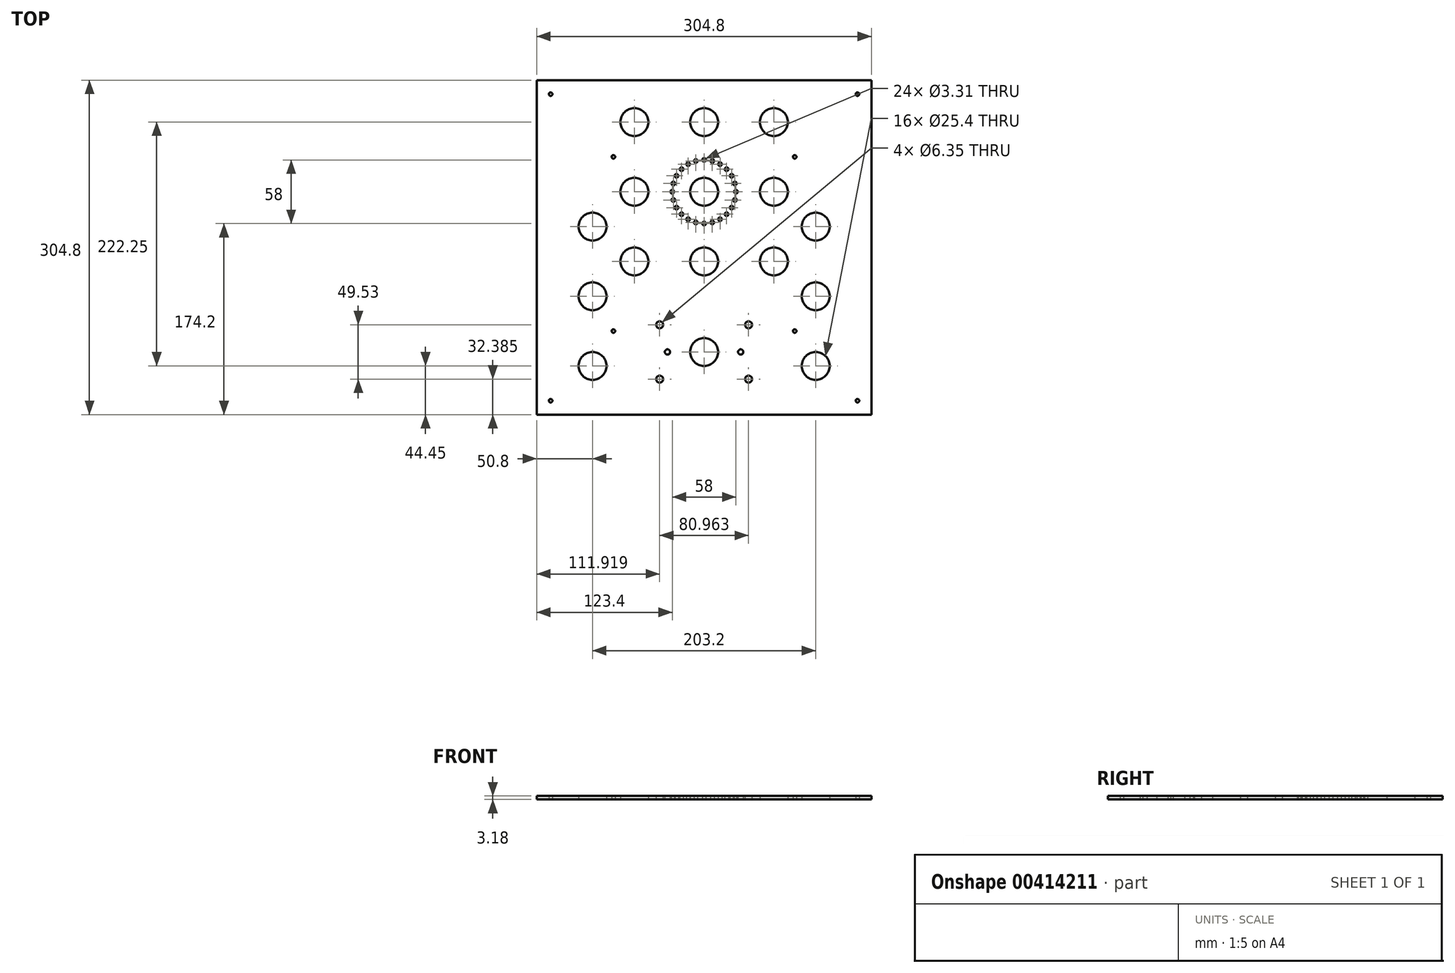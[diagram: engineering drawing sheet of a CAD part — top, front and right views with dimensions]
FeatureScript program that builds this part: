
annotation { "Feature Type Name" : "Feature", "Feature Type Description" : "" }
export const myFeature = defineFeature(function(context is Context, id is Id, definition is map)
    precondition{}
    {
        {
            var Q0;
            Q0=qCreatedBy(makeId("Top.planeOp"),FACE);
            var sketch = newSketch(context, id + "F0", { "sketchPlane" : qUnion([Q0])});
            skLineSegment(sketch, "E0.bottom", {"start": v(152.4, -152.4) * mm, "end": v(-152.4, -152.4) * mm});
            skLineSegment(sketch, "E0.top", {"start": v(152.4, 152.4) * mm, "end": v(-152.4, 152.4) * mm});
            skLineSegment(sketch, "E0.left", {"start": v(152.4, -152.4) * mm, "end": v(152.4, 152.4) * mm});
            skLineSegment(sketch, "E0.right", {"start": v(-152.4, -152.4) * mm, "end": v(-152.4, 152.4) * mm});
            skPoint(sketch, "E0.middle", {"position": v(0, 0) * mm});
            skCircle(sketch, "E1", {"center": v(0, -95.25) * mm, "radius": 12.7 * mm});
            skLineSegment(sketch, "E2.bottom", {"start": v(50.8, -133.35) * mm, "end": v(-50.8, -133.35) * mm, "construction": true});
            skLineSegment(sketch, "E2.top", {"start": v(50.8, -57.15) * mm, "end": v(-50.8, -57.15) * mm, "construction": true});
            skLineSegment(sketch, "E2.left", {"start": v(50.8, -133.35) * mm, "end": v(50.8, -57.15) * mm, "construction": true});
            skLineSegment(sketch, "E2.right", {"start": v(-50.8, -133.35) * mm, "end": v(-50.8, -57.15) * mm, "construction": true});
            skLineSegment(sketch, "E3.bottom", {"start": v(146.05, -146.05) * mm, "end": v(-146.05, -146.05) * mm, "construction": true});
            skLineSegment(sketch, "E3.top", {"start": v(146.05, 146.05) * mm, "end": v(-146.05, 146.05) * mm, "construction": true});
            skLineSegment(sketch, "E3.left", {"start": v(146.05, -146.05) * mm, "end": v(146.05, 146.05) * mm, "construction": true});
            skLineSegment(sketch, "E3.right", {"start": v(-146.05, -146.05) * mm, "end": v(-146.05, 146.05) * mm, "construction": true});
            skCircle(sketch, "E4", {"center": v(-63.5, 114.3) * mm, "radius": 12.7 * mm});
            skCircle(sketch, "E5.0.1.0", {"center": v(-63.5, 50.8) * mm, "radius": 12.7 * mm});
            skCircle(sketch, "E5.0.2.0", {"center": v(-63.5, -12.7) * mm, "radius": 12.7 * mm});
            skCircle(sketch, "E5.1.0.0", {"center": v(0, 114.3) * mm, "radius": 12.7 * mm});
            skCircle(sketch, "E5.1.1.0", {"center": v(0, 50.8) * mm, "radius": 12.7 * mm});
            skCircle(sketch, "E5.1.2.0", {"center": v(0, -12.7) * mm, "radius": 12.7 * mm});
            skCircle(sketch, "E5.2.0.0", {"center": v(63.5, 114.3) * mm, "radius": 12.7 * mm});
            skCircle(sketch, "E5.2.1.0", {"center": v(63.5, 50.8) * mm, "radius": 12.7 * mm});
            skCircle(sketch, "E5.2.2.0", {"center": v(63.5, -12.7) * mm, "radius": 12.7 * mm});
            skLineSegment(sketch, "E5.direction1", {"start": v(-63.5, 114.3) * mm, "end": v(0, 114.3) * mm, "construction": true});
            skLineSegment(sketch, "E5.direction2", {"start": v(-63.5, 114.3) * mm, "end": v(-63.5, 50.8) * mm, "construction": true});
            skCircle(sketch, "E6", {"center": v(-101.6, -107.95) * mm, "radius": 12.7 * mm});
            skCircle(sketch, "E7.0.1.0", {"center": v(-101.6, -44.45) * mm, "radius": 12.7 * mm});
            skCircle(sketch, "E7.0.2.0", {"center": v(-101.6, 19.05) * mm, "radius": 12.7 * mm});
            skCircle(sketch, "E7.1.0.0", {"center": v(101.6, -107.95) * mm, "radius": 12.7 * mm});
            skCircle(sketch, "E7.1.1.0", {"center": v(101.6, -44.45) * mm, "radius": 12.7 * mm});
            skCircle(sketch, "E7.1.2.0", {"center": v(101.6, 19.05) * mm, "radius": 12.7 * mm});
            skLineSegment(sketch, "E7.direction1", {"start": v(-101.6, -107.95) * mm, "end": v(101.6, -107.95) * mm, "construction": true});
            skLineSegment(sketch, "E7.direction2", {"start": v(-101.6, -107.95) * mm, "end": v(-101.6, -44.45) * mm, "construction": true});
            skPoint(sketch, "E8", {"position": v(0, -107.95) * mm});
            skCircle(sketch, "E9", {"center": v(0, 50.8) * mm, "radius": 33 * mm, "construction": true});
            skCircle(sketch, "E10", {"center": v(0, 50.8) * mm, "radius": 25.5 * mm, "construction": true});
            skCircle(sketch, "E11", {"center": v(0, 79.8) * mm, "radius": 1.66 * mm});
            skCircle(sketch, "E12.1.0", {"center": v(-7.5, 78.81) * mm, "radius": 1.66 * mm});
            skCircle(sketch, "E12.2.0", {"center": v(-14.5, 75.91) * mm, "radius": 1.66 * mm});
            skCircle(sketch, "E12.3.0", {"center": v(-20.5, 71.3) * mm, "radius": 1.66 * mm});
            skCircle(sketch, "E12.4.0", {"center": v(-25.11, 65.3) * mm, "radius": 1.66 * mm});
            skCircle(sketch, "E12.5.0", {"center": v(-28.01, 58.3) * mm, "radius": 1.66 * mm});
            skCircle(sketch, "E12.6.0", {"center": v(-29, 50.8) * mm, "radius": 1.66 * mm});
            skCircle(sketch, "E12.7.0", {"center": v(-28.01, 43.3) * mm, "radius": 1.66 * mm});
            skCircle(sketch, "E12.8.0", {"center": v(-25.11, 36.3) * mm, "radius": 1.66 * mm});
            skCircle(sketch, "E12.9.0", {"center": v(-20.5, 30.3) * mm, "radius": 1.66 * mm});
            skCircle(sketch, "E12.10.0", {"center": v(-14.5, 25.69) * mm, "radius": 1.66 * mm});
            skCircle(sketch, "E12.11.0", {"center": v(-7.5, 22.79) * mm, "radius": 1.66 * mm});
            skCircle(sketch, "E12.12.0", {"center": v(0, 21.8) * mm, "radius": 1.66 * mm});
            skCircle(sketch, "E12.13.0", {"center": v(7.5, 22.79) * mm, "radius": 1.66 * mm});
            skCircle(sketch, "E12.14.0", {"center": v(14.5, 25.69) * mm, "radius": 1.66 * mm});
            skCircle(sketch, "E12.15.0", {"center": v(20.5, 30.3) * mm, "radius": 1.66 * mm});
            skCircle(sketch, "E12.16.0", {"center": v(25.11, 36.3) * mm, "radius": 1.66 * mm});
            skCircle(sketch, "E12.17.0", {"center": v(28.01, 43.3) * mm, "radius": 1.66 * mm});
            skCircle(sketch, "E12.18.0", {"center": v(29, 50.8) * mm, "radius": 1.66 * mm});
            skCircle(sketch, "E12.19.0", {"center": v(28.01, 58.3) * mm, "radius": 1.66 * mm});
            skCircle(sketch, "E12.20.0", {"center": v(25.11, 65.3) * mm, "radius": 1.66 * mm});
            skCircle(sketch, "E12.21.0", {"center": v(20.5, 71.3) * mm, "radius": 1.66 * mm});
            skCircle(sketch, "E12.22.0", {"center": v(14.5, 75.91) * mm, "radius": 1.66 * mm});
            skCircle(sketch, "E12.23.0", {"center": v(7.5, 78.81) * mm, "radius": 1.66 * mm});
            skLineSegment(sketch, "E13", {"start": v(-33.34, -95.25) * mm, "end": v(33.34, -95.25) * mm, "construction": true});
            skCircle(sketch, "E14", {"center": v(-33.34, -95.25) * mm, "radius": 2.38 * mm});
            skCircle(sketch, "E15", {"center": v(33.34, -95.25) * mm, "radius": 2.38 * mm});
            skLineSegment(sketch, "E16", {"start": v(-40.48, -70.49) * mm, "end": v(-40.48, -120.02) * mm, "construction": true});
            skLineSegment(sketch, "E17", {"start": v(-40.48, -120.02) * mm, "end": v(40.48, -120.02) * mm, "construction": true});
            skLineSegment(sketch, "E18", {"start": v(40.48, -120.02) * mm, "end": v(40.48, -70.49) * mm, "construction": true});
            skLineSegment(sketch, "E19", {"start": v(40.48, -70.49) * mm, "end": v(-40.48, -70.49) * mm, "construction": true});
            skPoint(sketch, "E20", {"position": v(0, -70.49) * mm});
            skPoint(sketch, "E21", {"position": v(-40.48, -95.25) * mm});
            skCircle(sketch, "E22", {"center": v(-40.48, -70.49) * mm, "radius": 3.18 * mm});
            skCircle(sketch, "E23", {"center": v(40.48, -70.49) * mm, "radius": 3.18 * mm});
            skCircle(sketch, "E24", {"center": v(40.48, -120.02) * mm, "radius": 3.18 * mm});
            skCircle(sketch, "E25", {"center": v(-40.48, -120.02) * mm, "radius": 3.18 * mm});
            skLineSegment(sketch, "E26.bottom", {"start": v(-82.55, 82.55) * mm, "end": v(82.55, 82.55) * mm, "construction": true});
            skLineSegment(sketch, "E26.top", {"start": v(-82.55, -76.2) * mm, "end": v(82.55, -76.2) * mm, "construction": true});
            skLineSegment(sketch, "E26.left", {"start": v(-82.55, 82.55) * mm, "end": v(-82.55, -76.2) * mm, "construction": true});
            skLineSegment(sketch, "E26.right", {"start": v(82.55, 82.55) * mm, "end": v(82.55, -76.2) * mm, "construction": true});
            skPoint(sketch, "E27", {"position": v(0, 82.55) * mm});
            skPoint(sketch, "E28", {"position": v(-101.6, -76.2) * mm});
            skPoint(sketch, "E29", {"position": v(-63.5, 82.55) * mm});
            skLineSegment(sketch, "E30", {"start": v(-63.5, 50.8) * mm, "end": v(-63.5, -12.7) * mm, "construction": true});
            skLineSegment(sketch, "E31", {"start": v(-101.6, 19.05) * mm, "end": v(-63.5, 19.05) * mm, "construction": true});
            skPoint(sketch, "E32", {"position": v(-82.55, 19.05) * mm});
            skCircle(sketch, "E33", {"center": v(-82.55, 82.55) * mm, "radius": 1.59 * mm});
            skCircle(sketch, "E34", {"center": v(82.55, 82.55) * mm, "radius": 1.59 * mm});
            skCircle(sketch, "E35", {"center": v(82.55, -76.2) * mm, "radius": 1.59 * mm});
            skCircle(sketch, "E36", {"center": v(-82.55, -76.2) * mm, "radius": 1.59 * mm});
            skLineSegment(sketch, "E37", {"start": v(139.7, 146.05) * mm, "end": v(139.7, 139.7) * mm, "construction": true});
            skLineSegment(sketch, "E38", {"start": v(139.7, 139.7) * mm, "end": v(146.05, 139.7) * mm, "construction": true});
            skLineSegment(sketch, "E39", {"start": v(-146.05, 139.7) * mm, "end": v(-139.7, 139.7) * mm, "construction": true});
            skLineSegment(sketch, "E40", {"start": v(-139.7, 139.7) * mm, "end": v(-139.7, 146.05) * mm, "construction": true});
            skLineSegment(sketch, "E41", {"start": v(-146.05, -139.7) * mm, "end": v(-139.7, -139.7) * mm, "construction": true});
            skLineSegment(sketch, "E42", {"start": v(-139.7, -139.7) * mm, "end": v(-139.7, -146.05) * mm, "construction": true});
            skLineSegment(sketch, "E43", {"start": v(139.7, -146.05) * mm, "end": v(139.7, -139.7) * mm, "construction": true});
            skLineSegment(sketch, "E44", {"start": v(139.7, -139.7) * mm, "end": v(146.05, -139.7) * mm, "construction": true});
            skCircle(sketch, "E45", {"center": v(-139.7, 139.7) * mm, "radius": 1.59 * mm});
            skCircle(sketch, "E46", {"center": v(139.7, 139.7) * mm, "radius": 1.59 * mm});
            skCircle(sketch, "E47", {"center": v(139.7, -139.7) * mm, "radius": 1.59 * mm});
            skCircle(sketch, "E48", {"center": v(-139.7, -139.7) * mm, "radius": 1.59 * mm});
            skSolve(sketch);
        }
        {
            var Q0;
            Q0 = qSketchRegion(id + "F0", true);
            extrude(context, id + "F1", {"entities" : qUnion([Q0]), "depth" : 3.17 * mm});
        }
    });
